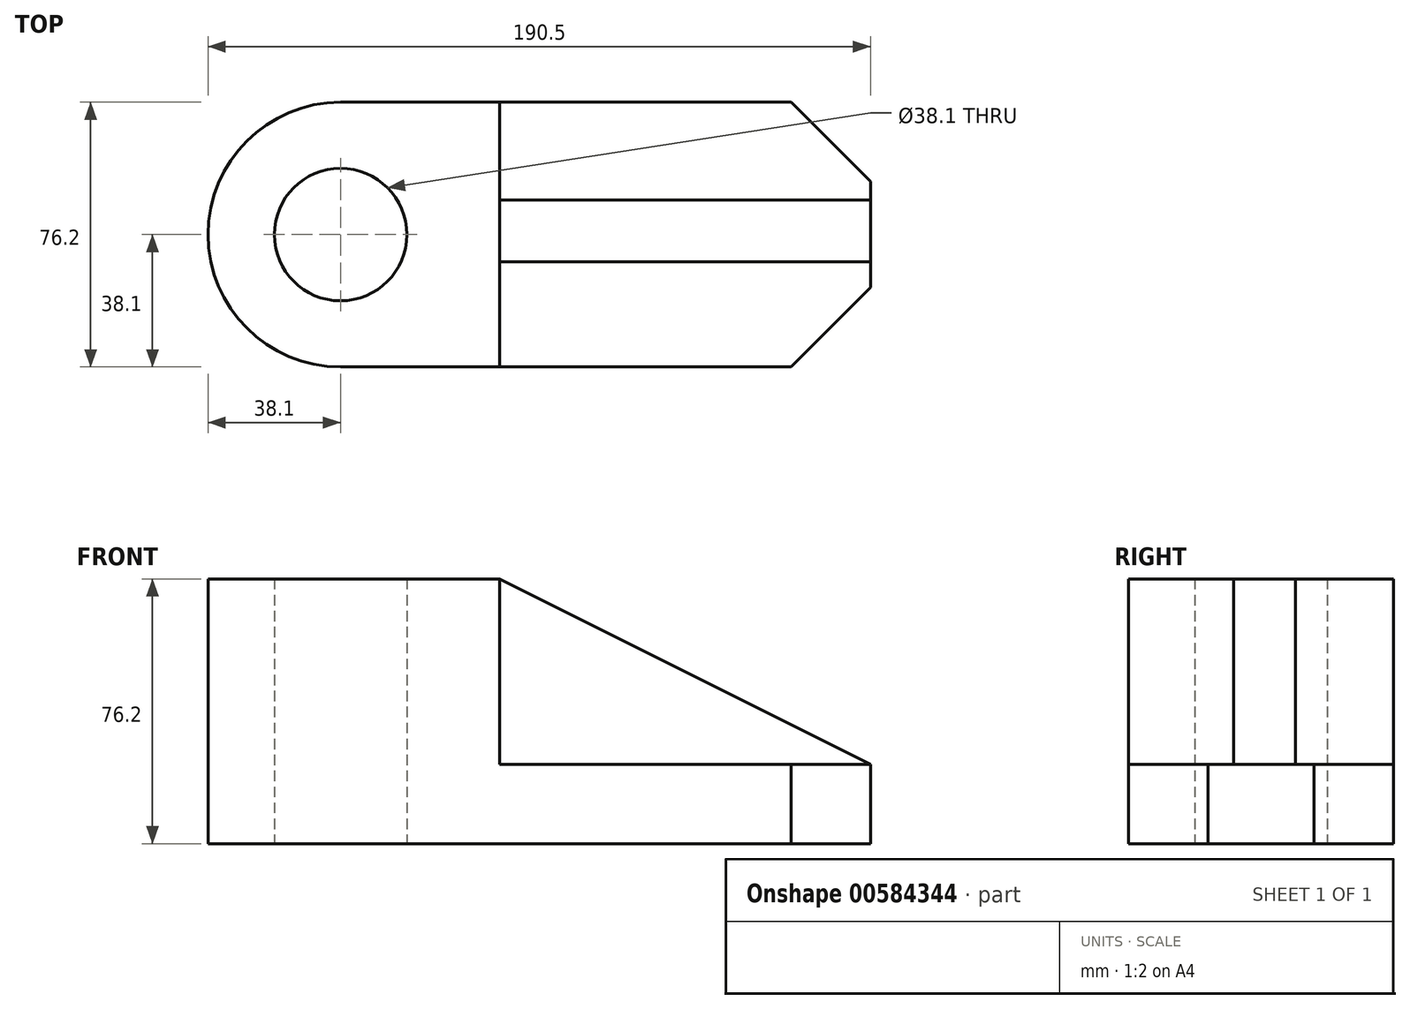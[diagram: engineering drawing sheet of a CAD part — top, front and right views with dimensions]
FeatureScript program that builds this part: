
annotation { "Feature Type Name" : "Feature", "Feature Type Description" : "" }
export const myFeature = defineFeature(function(context is Context, id is Id, definition is map)
    precondition{}
    {
        {
            var Q0;
            Q0=qCreatedBy(makeId("Top.planeOp"),FACE);
            var sketch = newSketch(context, id + "F0", { "sketchPlane" : qUnion([Q0])});
            skArc(sketch, "E0", {"start": v(0, 38.1) * mm, "mid": v(-38.1, 0) * mm, "end": v(0, -38.1) * mm});
            skCircle(sketch, "E1", {"center": v(0, 0) * mm, "radius": 19.05 * mm});
            skLineSegment(sketch, "E2", {"start": v(0, -38.1) * mm, "end": v(129.54, -38.1) * mm});
            skLineSegment(sketch, "E3", {"start": v(0, 38.1) * mm, "end": v(129.54, 38.1) * mm});
            skLineSegment(sketch, "E4", {"start": v(152.4, 15.24) * mm, "end": v(152.4, -15.24) * mm});
            skLineSegment(sketch, "E5", {"start": v(45.72, 38.1) * mm, "end": v(45.72, -38.1) * mm});
            skLineSegment(sketch, "E6", {"start": v(129.54, 38.1) * mm, "end": v(152.4, 15.24) * mm});
            skLineSegment(sketch, "E7", {"start": v(152.4, -15.24) * mm, "end": v(129.54, -38.1) * mm});
            skLineSegment(sketch, "E8", {"start": v(45.72, -7.83) * mm, "end": v(152.4, -7.83) * mm});
            skLineSegment(sketch, "E9", {"start": v(45.72, 9.95) * mm, "end": v(152.4, 9.95) * mm});
            skPoint(sketch, "E10.orphan", {"position": v(152.4, 38.1) * mm});
            skPoint(sketch, "E11.orphan", {"position": v(152.4, -38.1) * mm});
            skSolve(sketch);
        }
        {
            var Q0;
            {var subQ1=sQuery(id+"F0.wireOp",EDGE,"E0");Q0=makeQuery(id+"F0.imprint","IMPRINT",FACE,{"disambiguationData":[TD([[makeQuery(id+"F0.imprint","IMPRINT",EDGE,{"derivedFrom":subQ1}),1.0]])]});}
            var Q1;
            {var subQ0=sQuery(id+"F0.wireOp",EDGE,"E8");Q1=makeQuery(id+"F0.imprint","IMPRINT",FACE,{"disambiguationData":[TD([[makeQuery(id+"F0.imprint","IMPRINT",EDGE,{"derivedFrom":subQ0}),1.0]])]});}
            extrude(context, id + "F1", {"entities" : qUnion([Q0, Q1]), "depth" : 76.2 * mm, "offsetDistance" : 25.4 * mm});
        }
        {
            var Q0;
            {var subQ4=sQuery(id+"F0.wireOp",EDGE,"E7");Q0=makeQuery(id+"F0.imprint","IMPRINT",FACE,{"disambiguationData":[TD([[makeQuery(id+"F0.imprint","IMPRINT",EDGE,{"derivedFrom":subQ4}),-1.0]])]});}
            var Q1;
            {var subQ0=sQuery(id+"F0.wireOp",EDGE,"E6");Q1=makeQuery(id+"F0.imprint","IMPRINT",FACE,{"disambiguationData":[TD([[makeQuery(id+"F0.imprint","IMPRINT",EDGE,{"derivedFrom":subQ0}),-1.0]])]});}
            extrude(context, id + "F2", {"entities" : qUnion([Q0, Q1]), "operationType" : NewBodyOperationType.ADD, "depth" : 22.86 * mm, "offsetDistance" : 25.4 * mm});
        }
        {
            var Q0;
            Q0=makeQuery(id+"F1.opExtrude","SWEPT_FACE",FACE,{"disambiguationData":[OSD([sQuery(id+"F0.wireOp",EDGE,"E8")])]});
            var sketch = newSketch(context, id + "F3", { "sketchPlane" : qUnion([Q0])});
            skLineSegment(sketch, "E12", {"start": v(45.72, 76.2) * mm, "end": v(152.4, 22.86) * mm});
            skSolve(sketch);
        }
        {
            var Q0;
            Q0 = qSketchRegion(id + "F3", true);
            var Q1;
            Q1=makeQuery(id+"F3.imprint","IMPRINT",FACE,{"disambiguationData":[TD([[makeQuery(id+"F3.imprint","IMPRINT",EDGE,{"derivedFrom":sQuery(id+"F3.wireOp",EDGE,"E12")}),1.0]])]});
            extrude(context, id + "F4", {"entities" : qUnion([Q0, Q1]), "operationType" : NewBodyOperationType.REMOVE, "oppositeDirection" : true, "depth" : 25.4 * mm, "offsetDistance" : 25.4 * mm});
        }
    });
